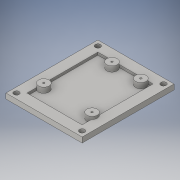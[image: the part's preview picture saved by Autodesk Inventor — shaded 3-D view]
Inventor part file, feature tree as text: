
AUTODESK INVENTOR PART (.ipt)
format: ipt  version: 2016 (Build 200138000, 138)  size: 176,128 bytes
history: native  units: in
note: dims shown in document units (in); Inventor stores cm internally (conversion verified against a paired STEP export)
features: sketch x8, hole x5, extrude x3
ambient origin geometry x8: Origin, YZ Plane, XZ Plane, XY Plane, X Axis, Y Axis, Z Axis, Center Point
bodies: Solid1 (feature_tree)
feature tree (16):
  extrude  "Extrusion1"  Depth=2.1in
  extrude  "Extrusion2"  Depth=0.4in
  hole  "Hole1"  [1 undecoded]
  extrude  "Extrusion3"  Depth=0.2in TaperAngle=0.0deg
  hole  "Hole2"  [1 undecoded]
  hole  "Hole3"  [1 undecoded]
  hole  "Hole4"  [1 undecoded]
  hole  "Hole5"  [1 undecoded]
  sketch  "Sketch1"  dims[d0=2.7in d1=2.1in]
  sketch  "Sketch2"  dims[d2=0.1in d3=0.0in d4=0.4in]
  sketch  "Sketch3"  dims[d5=0.4in d6=0.4in]
  sketch  "Sketch4"  dims[d7=0.4in d8=0.2in d9=0.0in]
  sketch  "Sketch5"  dims[d10=0.2in d11=0.2in]
  sketch  "Sketch6"  dims[d12=0.0in d13=0.2in]
  sketch  "Sketch7"  dims[d14=0.0in d15=0.0in]
  sketch  "Sketch8"  dims[d16=0.2in d17=0.0in d18=0.2in d19=0.75in d20=0.375in d21=0.25in d22=0.5635in d23=1.0in d24=0.8108in d25=0.4in d26=0.4in d27=0.4in d28=0.4in d36=1.0984in d41=2.0433in d42=2.0in d43=0.5984in d44=0.0in d45=0.1299in d46=0.185in d47=0.5512in d48=0.2in d49=0.0in d50=0.07in d51=0.75in d52=0.375in d53=0.25in d54=0.5635in d55=1.0in d56=0.8108in d57=0.07in d58=0.75in d59=0.375in d60=0.25in d61=0.5635in d62=1.0in d63=0.8108in d64=0.07in d65=0.75in d66=0.375in d67=0.25in d68=0.5635in d69=1.0in d70=0.8108in d71=0.07in d72=0.75in d73=0.375in d74=0.25in d75=0.5635in d76=1.0in d77=0.8108in]
note: 5 required parameter values undecoded (feature->parameter linkage not recoverable at this tier; creation-order binding heuristic only, values carry confidence <= 0.55)
